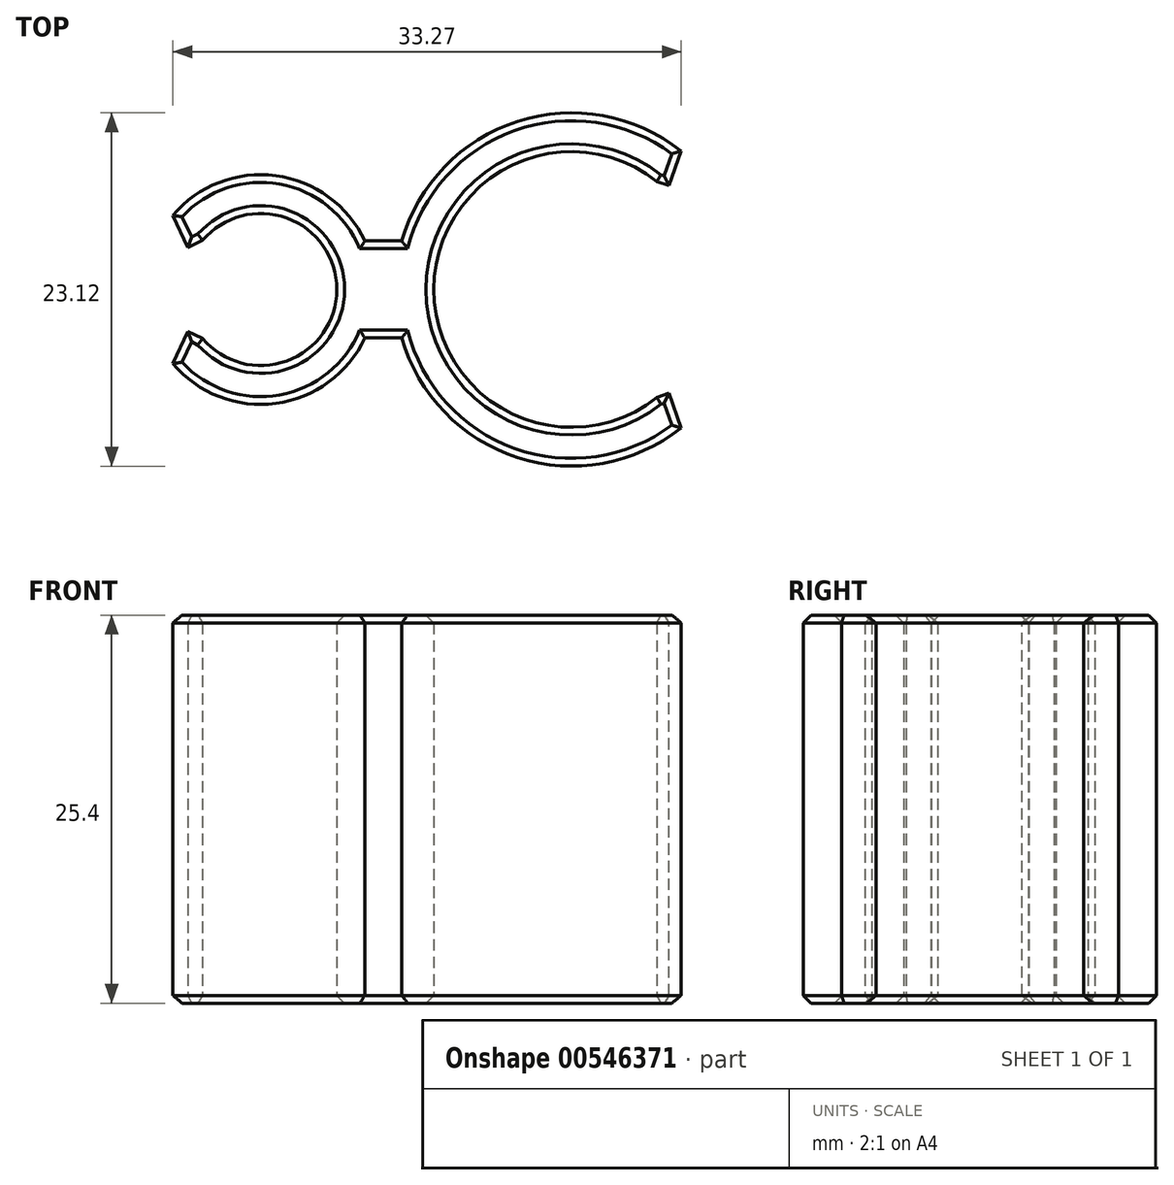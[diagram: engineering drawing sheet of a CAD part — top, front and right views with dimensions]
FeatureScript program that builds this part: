
annotation { "Feature Type Name" : "Feature", "Feature Type Description" : "" }
export const myFeature = defineFeature(function(context is Context, id is Id, definition is map)
    precondition{}
    {
        {
            var Q0;
            Q0=qCreatedBy(makeId("Top.planeOp"),FACE);
            var sketch = newSketch(context, id + "F0", { "sketchPlane" : qUnion([Q0])});
            skArc(sketch, "E0", {"start": v(-4.15, -2.76) * mm, "mid": v(4.98, 0) * mm, "end": v(-4.15, 2.76) * mm});
            skArc(sketch, "E1", {"start": v(26.27, 6.8) * mm, "mid": v(11.33, 0) * mm, "end": v(26.27, -6.8) * mm});
            skArc(sketch, "E2.0", {"start": v(9.23, -3.17) * mm, "mid": v(18.33, -11.38) * mm, "end": v(29.7, -6.8) * mm});
            skArc(sketch, "E3.0", {"start": v(6.82, 3.18) * mm, "mid": v(-0.23, 7.51) * mm, "end": v(-7, 2.76) * mm});
            skLineSegment(sketch, "E4", {"start": v(6.82, -3.18) * mm, "end": v(9.23, -3.18) * mm});
            skLineSegment(sketch, "E5", {"start": v(6.82, 3.18) * mm, "end": v(9.23, 3.18) * mm});
            skLineSegment(sketch, "E6", {"start": v(-4.15, 2.76) * mm, "end": v(-7, 2.76) * mm});
            skLineSegment(sketch, "E7", {"start": v(-4.15, -2.76) * mm, "end": v(-7, -2.76) * mm});
            skArc(sketch, "E8.trimOffspring", {"start": v(-7, -2.76) * mm, "mid": v(-0.23, -7.51) * mm, "end": v(6.82, -3.18) * mm});
            skLineSegment(sketch, "E9", {"start": v(29.7, 6.8) * mm, "end": v(26.27, 6.8) * mm});
            skLineSegment(sketch, "E10", {"start": v(29.7, -6.8) * mm, "end": v(26.27, -6.8) * mm});
            skArc(sketch, "E11.trimOffspring", {"start": v(29.7, 6.8) * mm, "mid": v(18.33, 11.38) * mm, "end": v(9.23, 3.17) * mm});
            skSolve(sketch);
        }
        {
            var Q0;
            Q0=makeQuery(id+"F0.imprint","IMPRINT",FACE,{"disambiguationData":[TD([[makeQuery(id+"F0.imprint","IMPRINT",EDGE,{"derivedFrom":sQuery(id+"F0.wireOp",EDGE,"E0")}),-1.0]])]});
            extrude(context, id + "F1", {"entities" : qUnion([Q0]), "depth" : 25.4 * mm, "offsetDistance" : 25.4 * mm});
        }
        {
            var Q0;
            Q0=makeQuery(id+"F1.opExtrude","SWEPT_EDGE",EDGE,{"disambiguationData":[OSD([sQuery(id+"F0.wireOp",EDGE,"E7"),sQuery(id+"F0.wireOp",EDGE,"E8.trimOffspring")])]});
            var Q1;
            Q1=makeQuery(id+"F1.opExtrude","SWEPT_EDGE",EDGE,{"disambiguationData":[OSD([sQuery(id+"F0.wireOp",EDGE,"E3.0"),sQuery(id+"F0.wireOp",EDGE,"E6")])]});
            var Q2;
            Q2=makeQuery(id+"F1.opExtrude","SWEPT_EDGE",EDGE,{"disambiguationData":[OSD([sQuery(id+"F0.wireOp",EDGE,"E0"),sQuery(id+"F0.wireOp",EDGE,"E6")])]});
            var Q3;
            Q3=makeQuery(id+"F1.opExtrude","SWEPT_EDGE",EDGE,{"disambiguationData":[OSD([sQuery(id+"F0.wireOp",EDGE,"E0"),sQuery(id+"F0.wireOp",EDGE,"E7")])]});
            var Q4;
            Q4=makeQuery(id+"F1.opExtrude","SWEPT_EDGE",EDGE,{"disambiguationData":[OSD([sQuery(id+"F0.wireOp",EDGE,"E2.0"),sQuery(id+"F0.wireOp",EDGE,"E10")])]});
            var Q5;
            Q5=makeQuery(id+"F1.opExtrude","SWEPT_EDGE",EDGE,{"disambiguationData":[OSD([sQuery(id+"F0.wireOp",EDGE,"E1"),sQuery(id+"F0.wireOp",EDGE,"E10")])]});
            var Q6;
            Q6=makeQuery(id+"F1.opExtrude","SWEPT_EDGE",EDGE,{"disambiguationData":[OSD([sQuery(id+"F0.wireOp",EDGE,"E1"),sQuery(id+"F0.wireOp",EDGE,"E9")])]});
            var Q7;
            Q7=makeQuery(id+"F1.opExtrude","SWEPT_EDGE",EDGE,{"disambiguationData":[OSD([sQuery(id+"F0.wireOp",EDGE,"E9"),sQuery(id+"F0.wireOp",EDGE,"E11.trimOffspring")])]});
            chamfer(context, id + "F2", {"entities" : qUnion([Q0, Q1, Q2, Q3, Q4, Q5, Q6, Q7]), "width" : 1.27 * mm, "tangentPropagation" : true});
        }
        {
            var Q0;
            Q0=makeQuery(id+"F1.opExtrude","CAP_FACE",FACE,{"disambiguationData":[OSD([sQuery(id+"F0.wireOp",EDGE,"E0"),sQuery(id+"F0.wireOp",EDGE,"E1"),sQuery(id+"F0.wireOp",EDGE,"E2.0"),sQuery(id+"F0.wireOp",EDGE,"E3.0"),sQuery(id+"F0.wireOp",EDGE,"E4"),sQuery(id+"F0.wireOp",EDGE,"E5"),sQuery(id+"F0.wireOp",EDGE,"E6"),sQuery(id+"F0.wireOp",EDGE,"E7"),sQuery(id+"F0.wireOp",EDGE,"E8.trimOffspring"),sQuery(id+"F0.wireOp",EDGE,"E9"),sQuery(id+"F0.wireOp",EDGE,"E10"),sQuery(id+"F0.wireOp",EDGE,"E11.trimOffspring")])],"isStart":false});
            var Q1;
            Q1=makeQuery(id+"F1.opExtrude","CAP_FACE",FACE,{"disambiguationData":[OSD([sQuery(id+"F0.wireOp",EDGE,"E0"),sQuery(id+"F0.wireOp",EDGE,"E1"),sQuery(id+"F0.wireOp",EDGE,"E2.0"),sQuery(id+"F0.wireOp",EDGE,"E3.0"),sQuery(id+"F0.wireOp",EDGE,"E4"),sQuery(id+"F0.wireOp",EDGE,"E5"),sQuery(id+"F0.wireOp",EDGE,"E6"),sQuery(id+"F0.wireOp",EDGE,"E7"),sQuery(id+"F0.wireOp",EDGE,"E8.trimOffspring"),sQuery(id+"F0.wireOp",EDGE,"E9"),sQuery(id+"F0.wireOp",EDGE,"E10"),sQuery(id+"F0.wireOp",EDGE,"E11.trimOffspring")])],"isStart":true});
            chamfer(context, id + "F3", {"entities" : qUnion([Q0, Q1]), "width" : 0.5 * mm, "tangentPropagation" : true});
        }
    });
